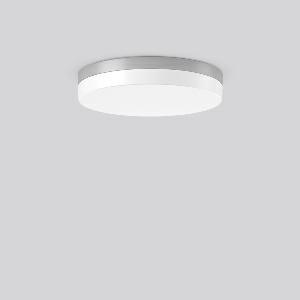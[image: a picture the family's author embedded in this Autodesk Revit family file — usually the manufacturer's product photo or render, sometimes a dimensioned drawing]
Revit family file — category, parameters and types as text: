
# Revit family: flat_slim_round_312675_004_19_11cc
name_source: partatom
category: Lighting Fixtures
units: mm (PartAtom-declared; Revit-internal decimal feet)

## family parameters
Cut with Voids When Loaded = No
Host = Face
Light Source = No
Part Type = Normal
Room Calculation Point = No
Round Connector Dimension = Use Diameter
Shared = No

## types (1)
- MultiLumen 1 830 (1 x LED Modul 830, 2450 lm, 3000)
    Apparent Load = 25 VA
    CIE Flux Codes = 40 70 90 84 100
    Color Rendering = 80
    Color Temperature = 3000
    Default Elevation = 1800 mm
    Height = 75 mm
    Lamp = 1 x LED Modul 830
    Lamp Light Flux = 2450 lm
    Lamp count = 1
    Length = 400 mm
    Lifetime = 50000 h
    Luminous efficacy = 98 lm/W
    Manufacturer = RZB
    ModVariant = No
    Model = 312675.004.19
    Mounting Place = Ceiling
    Mounting Type = Surface mounted
    Number of Poles = 1
    OnlyDefault = Yes
    Power Factor = 1
    Product Name = FLAT SLIM round
    Product group = Surface mounted ceiling and wall luminaires
    ProductGroupID = 305
    Protection Class = Protection class I
    Protection Degree = Degree of protection
    RLX_Detail_Level = 1
    RLX_Emergency_Light_Flux = 0 lm
    RLX_Emergency_Type = 0
    RLX_Emergency_Type_DB = No
    RlxData = <blob elided: 20829 chars, md5=57a8dc95>
    Socket = socket
    Standby Power = 0 W
    System Light Flux = 2450 lm
    System Power = 25 W
    Type Comments = MultiLumen 1 830
    Type Image = 312631.004.jpg
    URL = http://relux.com
    VarID = multilumen_1_830
    Voltage = 0 V
    Weight = 0.00 kg
    Width = 0 mm  [stored 0 ft]

note: [stored X ft] marks values corroborated as IEEE doubles in the binary element streams (Revit-internal decimal feet)

## geometry (parser evidence)
native form markers: Blend x4, Sweep x13
no freeform markers — native parametric forms only
